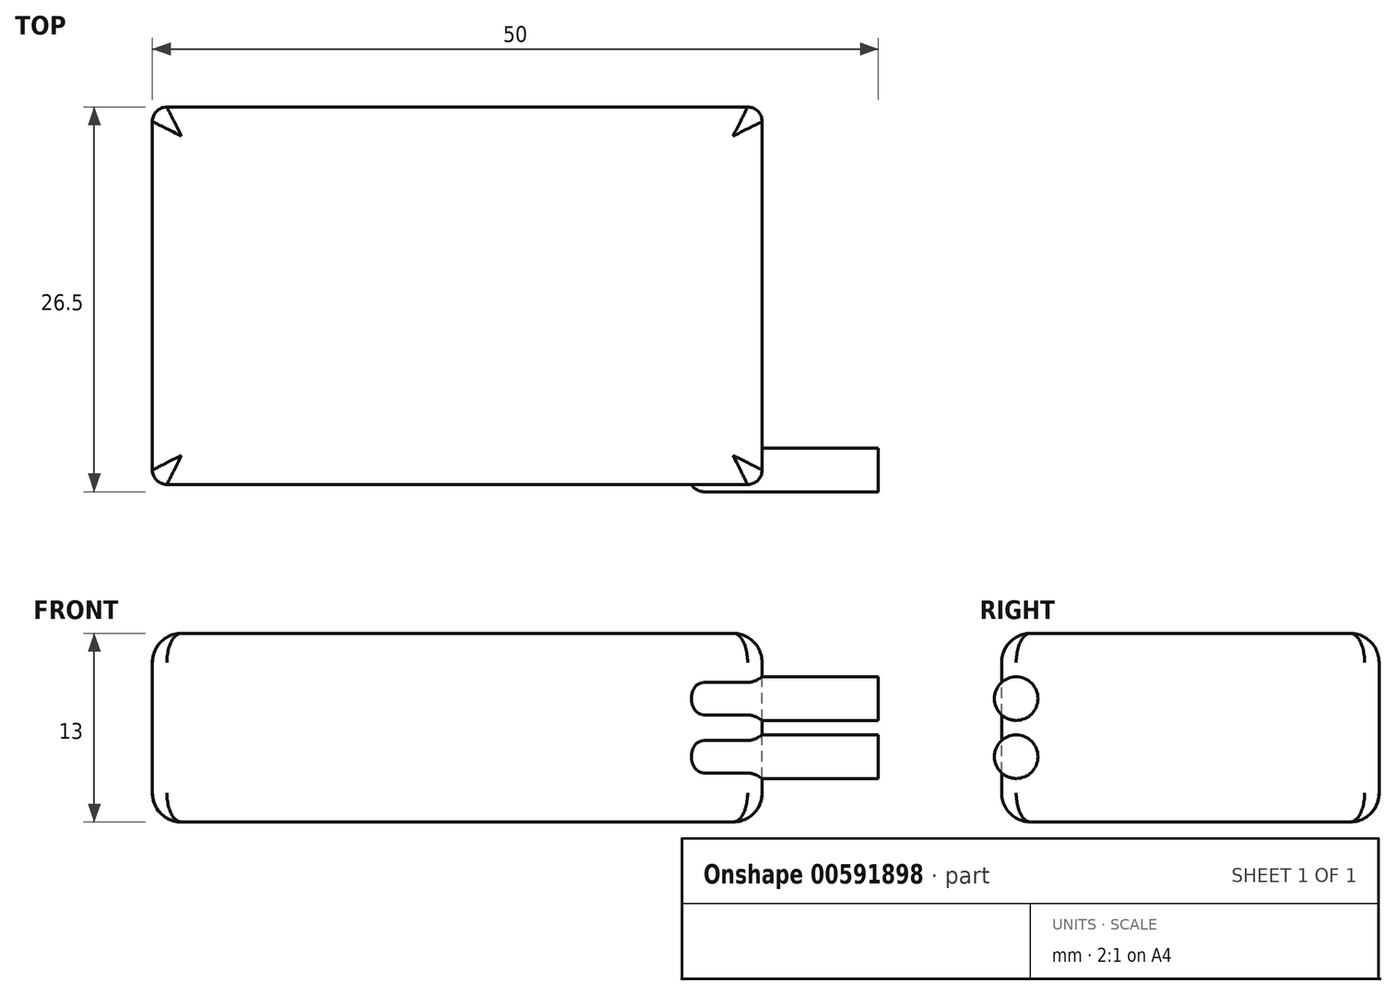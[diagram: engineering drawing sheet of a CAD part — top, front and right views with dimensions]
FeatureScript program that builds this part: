
annotation { "Feature Type Name" : "Feature", "Feature Type Description" : "" }
export const myFeature = defineFeature(function(context is Context, id is Id, definition is map)
    precondition{}
    {
        {
            var Q0;
            Q0=qCreatedBy(makeId("Top.planeOp"),FACE);
            var sketch = newSketch(context, id + "F0", { "sketchPlane" : qUnion([Q0])});
            skLineSegment(sketch, "E0.bottom", {"start": v(21, 13) * mm, "end": v(-21, 13) * mm});
            skLineSegment(sketch, "E0.top", {"start": v(21, -13) * mm, "end": v(-21, -13) * mm});
            skLineSegment(sketch, "E0.left", {"start": v(21, 13) * mm, "end": v(21, -13) * mm});
            skLineSegment(sketch, "E0.right", {"start": v(-21, 13) * mm, "end": v(-21, -13) * mm});
            skPoint(sketch, "E0.middle", {"position": v(0, 0) * mm});
            skSolve(sketch);
        }
        {
            var Q0;
            Q0 = qSketchRegion(id + "F0", true);
            extrude(context, id + "F1", {"entities" : qUnion([Q0]), "depth" : 13 * mm, "offsetDistance" : 25 * mm, "symmetric" : true});
        }
        {
            var Q0;
            Q0=makeQuery(id+"F1.opExtrude","CAP_FACE",FACE,{"disambiguationData":[OSD([sQuery(id+"F0.wireOp",EDGE,"E0.bottom"),sQuery(id+"F0.wireOp",EDGE,"E0.top"),sQuery(id+"F0.wireOp",EDGE,"E0.left"),sQuery(id+"F0.wireOp",EDGE,"E0.right")])],"isStart":false});
            var Q1;
            Q1=makeQuery(id+"F1.opExtrude","CAP_FACE",FACE,{"disambiguationData":[OSD([sQuery(id+"F0.wireOp",EDGE,"E0.bottom"),sQuery(id+"F0.wireOp",EDGE,"E0.top"),sQuery(id+"F0.wireOp",EDGE,"E0.left"),sQuery(id+"F0.wireOp",EDGE,"E0.right")])],"isStart":true});
            fillet(context, id + "F2", {"entities" : qUnion([Q0, Q1]), "radius" : 2 * mm, "tangentPropagation" : true, "allowEdgeOverflow" : false});
        }
        {
            var Q0;
            Q0=makeQuery(id+"F1.opExtrude","SWEPT_EDGE",EDGE,{"disambiguationData":[OSD([sQuery(id+"F0.wireOp",EDGE,"E0.top"),sQuery(id+"F0.wireOp",EDGE,"E0.left")])]});
            var Q1;
            Q1=makeQuery(id+"F1.opExtrude","SWEPT_EDGE",EDGE,{"disambiguationData":[OSD([sQuery(id+"F0.wireOp",EDGE,"E0.top"),sQuery(id+"F0.wireOp",EDGE,"E0.right")])]});
            var Q2;
            Q2=makeQuery(id+"F1.opExtrude","SWEPT_EDGE",EDGE,{"disambiguationData":[OSD([sQuery(id+"F0.wireOp",EDGE,"E0.bottom"),sQuery(id+"F0.wireOp",EDGE,"E0.left")])]});
            var Q3;
            Q3=makeQuery(id+"F1.opExtrude","SWEPT_EDGE",EDGE,{"disambiguationData":[OSD([sQuery(id+"F0.wireOp",EDGE,"E0.bottom"),sQuery(id+"F0.wireOp",EDGE,"E0.right")])]});
            fillet(context, id + "F3", {"entities" : qUnion([Q0, Q1, Q2, Q3]), "radius" : 1 * mm, "tangentPropagation" : true, "allowEdgeOverflow" : false});
        }
        {
            var Q0;
            Q0=makeQuery(id+"F1.opExtrude","SWEPT_FACE",FACE,{"disambiguationData":[OSD([sQuery(id+"F0.wireOp",EDGE,"E0.left")])]});
            var sketch = newSketch(context, id + "F4", { "sketchPlane" : qUnion([Q0])});
            skCircle(sketch, "E1", {"center": v(-12, 2) * mm, "radius": 1.5 * mm});
            skCircle(sketch, "E2", {"center": v(-12, -2) * mm, "radius": 1.5 * mm});
            skLineSegment(sketch, "E3", {"start": v(-12, 2) * mm, "end": v(-12, -2) * mm, "construction": true});
            skPoint(sketch, "E4", {"position": v(-12, 0) * mm});
            skSolve(sketch);
        }
        {
            var Q0;
            Q0 = qSketchRegion(id + "F4", true);
            extrude(context, id + "F5", {"entities" : qUnion([Q0]), "operationType" : NewBodyOperationType.ADD, "depth" : 8 * mm, "offsetDistance" : 25 * mm, "hasSecondDirection" : true, "secondDirectionOppositeDirection" : true, "secondDirectionDepth" : 5 * mm});
        }
        {
            var Q0;
            Q0=makeQuery(id+"F5.opExtrude","CAP_EDGE",EDGE,{"disambiguationData":[OSD([sQuery(id+"F4.wireOp",EDGE,"E1")])],"isStart":true});
            var Q1;
            Q1=makeQuery(id+"F5.opExtrude","CAP_EDGE",EDGE,{"disambiguationData":[OSD([sQuery(id+"F4.wireOp",EDGE,"E2")])],"isStart":true});
            fillet(context, id + "F6", {"entities" : qUnion([Q0, Q1]), "radius" : 1 * mm, "tangentPropagation" : true, "allowEdgeOverflow" : false});
        }
    });
